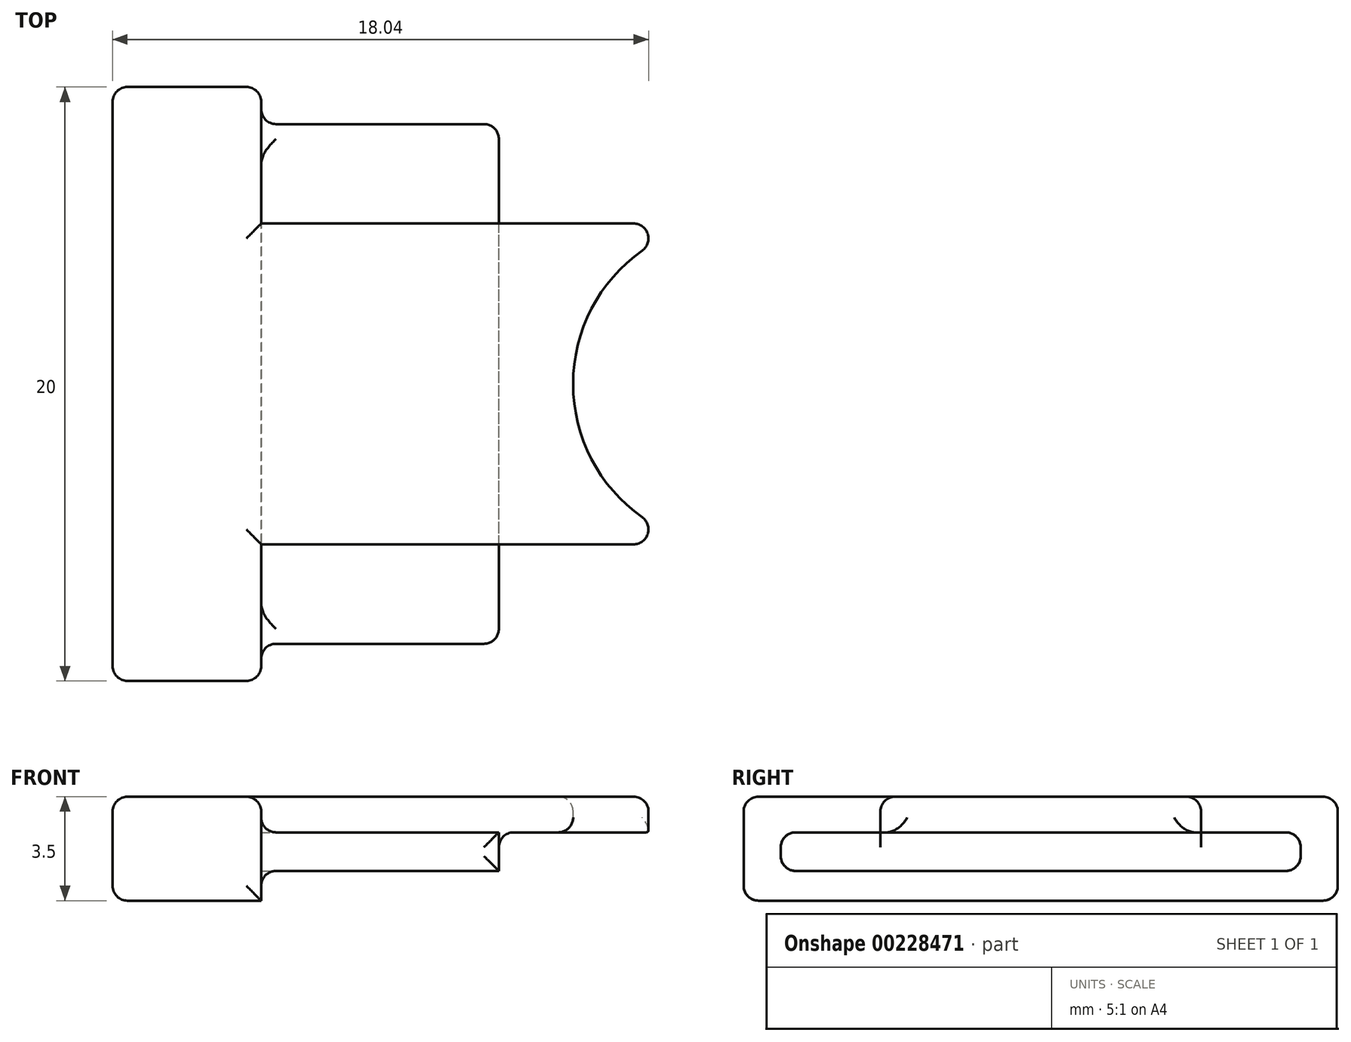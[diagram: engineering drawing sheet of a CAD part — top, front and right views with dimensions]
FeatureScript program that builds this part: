
annotation { "Feature Type Name" : "Feature", "Feature Type Description" : "" }
export const myFeature = defineFeature(function(context is Context, id is Id, definition is map)
    precondition{}
    {
        {
            var Q0;
            Q0=qCreatedBy(makeId("Right.planeOp"),FACE);
            var sketch = newSketch(context, id + "F0", { "sketchPlane" : qUnion([Q0])});
            skLineSegment(sketch, "E0", {"start": v(14.15, 2.5) * mm, "end": v(14.15, 1.3) * mm});
            skLineSegment(sketch, "E1", {"start": v(14.15, 1.3) * mm, "end": v(17.5, 1.3) * mm});
            skLineSegment(sketch, "E2", {"start": v(17.5, 1.3) * mm, "end": v(17.5, 0) * mm});
            skLineSegment(sketch, "E3", {"start": v(17.5, 0) * mm, "end": v(0, 0) * mm});
            skLineSegment(sketch, "E4", {"start": v(0, 0) * mm, "end": v(0, 1.3) * mm});
            skLineSegment(sketch, "E5", {"start": v(0, 1.3) * mm, "end": v(3.35, 1.3) * mm});
            skLineSegment(sketch, "E6", {"start": v(3.35, 1.3) * mm, "end": v(3.35, 2.5) * mm});
            skLineSegment(sketch, "E7", {"start": v(3.35, 2.5) * mm, "end": v(14.15, 2.5) * mm});
            skSolve(sketch);
        }
        {
            var Q0;
            Q0=qSketchRegion(id+"F0",true);
            extrude(context, id + "F1", {"entities" : qUnion([Q0]), "depth" : 16 * mm});
        }
        {
            var Q0;
            Q0=makeQuery(id+"F1.opExtrude","CAP_FACE",FACE,{"disambiguationData":[OSD([sQuery(id+"F0.wireOp",EDGE,"TZ5eURmr-gxjI-tz5t-PajN-iYrOHizqFekN"),sQuery(id+"F0.wireOp",EDGE,"guARKJ44-jrx5-pMLB-4T0B-qmOtUb4eJ82T"),sQuery(id+"F0.wireOp",EDGE,"9YoBGH4t-UvKz-ujqG-odl2-F9yTLTpAYBFK"),sQuery(id+"F0.wireOp",EDGE,"E0"),sQuery(id+"F0.wireOp",EDGE,"E1"),sQuery(id+"F0.wireOp",EDGE,"E2"),sQuery(id+"F0.wireOp",EDGE,"E3"),sQuery(id+"F0.wireOp",EDGE,"E4"),sQuery(id+"F0.wireOp",EDGE,"E5"),sQuery(id+"F0.wireOp",EDGE,"E6"),sQuery(id+"F0.wireOp",EDGE,"JbcaB8nq-M2Nf-0EEa-IcCz-uRVHlxThzm4p"),sQuery(id+"F0.wireOp",EDGE,"coUqNx9z-0dZS-eHZ1-lRqT-18s0Kbs40iIy")])],"isStart":true});
            var sketch = newSketch(context, id + "F2", { "sketchPlane" : qUnion([Q0])});
            skLineSegment(sketch, "E8.bottom", {"start": v(1.25, -1) * mm, "end": v(-18.75, -1) * mm});
            skLineSegment(sketch, "E8.top", {"start": v(1.25, 2.5) * mm, "end": v(-18.75, 2.5) * mm});
            skLineSegment(sketch, "E8.left", {"start": v(1.25, -1) * mm, "end": v(1.25, 2.5) * mm});
            skLineSegment(sketch, "E8.right", {"start": v(-18.75, -1) * mm, "end": v(-18.75, 2.5) * mm});
            skSolve(sketch);
        }
        {
            var Q0;
            Q0=qSketchRegion(id+"F2",true);
            extrude(context, id + "F3", {"entities" : qUnion([Q0]), "operationType" : NewBodyOperationType.ADD, "depth" : 5 * mm});
        }
        {
            var Q0;
            Q0=makeQuery(id+"F3.boolean.opBoolean","MERGE",FACE,{"derivedFrom":[makeQuery(id+"F1.opExtrude","SWEPT_FACE",FACE,{"disambiguationData":[OSD([sQuery(id+"F0.wireOp",EDGE,"9YoBGH4t-UvKz-ujqG-odl2-F9yTLTpAYBFK")])]}),makeQuery(id+"F1.opExtrude","SWEPT_FACE",FACE,{"disambiguationData":[OSD([sQuery(id+"F0.wireOp",EDGE,"coUqNx9z-0dZS-eHZ1-lRqT-18s0Kbs40iIy")])]}),makeQuery(id+"F3.opExtrude","SWEPT_FACE",FACE,{"disambiguationData":[OSD([sQuery(id+"F2.wireOp",EDGE,"E8.top")])]})]});
            var sketch = newSketch(context, id + "F4", { "sketchPlane" : qUnion([Q0])});
            skPoint(sketch, "E9", {"position": v(16, 8.75) * mm});
            skLineSegment(sketch, "E10", {"start": v(16.03, 3.25) * mm, "end": v(16, 14.25) * mm});
            skArc(sketch, "E11", {"start": v(16, 14.25) * mm, "mid": v(10.5, 8.74) * mm, "end": v(16.03, 3.25) * mm});
            skSolve(sketch);
        }
        {
            var Q0;
            Q0=qSketchRegion(id+"F4",true);
            extrude(context, id + "F5", {"entities" : qUnion([Q0]), "operationType" : NewBodyOperationType.REMOVE, "oppositeDirection" : true, "depth" : 5 * mm});
        }
        {
            var Q0;
            {var subQ0=sQuery(id+"F0.wireOp",EDGE,"E3");var subQ1=sQuery(id+"F0.wireOp",EDGE,"E4");var subQ2=sQuery(id+"F0.wireOp",EDGE,"E5");Q0=makeQuery(id+"F5.boolean.opBoolean","SPLIT",FACE,{"disambiguationData":[TD([makeQuery(id+"F1.opExtrude","SWEPT_FACE",FACE,{"disambiguationData":[OSD([subQ1])]})])],"derivedFrom":makeQuery(id+"F1.opExtrude","CAP_FACE",FACE,{"disambiguationData":[OSD([sQuery(id+"F0.wireOp",EDGE,"E0"),sQuery(id+"F0.wireOp",EDGE,"E1"),sQuery(id+"F0.wireOp",EDGE,"E2"),subQ0,subQ1,subQ2,sQuery(id+"F0.wireOp",EDGE,"E6"),sQuery(id+"F0.wireOp",EDGE,"E7")])],"isStart":false})});}
            var sketch = newSketch(context, id + "F6", { "sketchPlane" : qUnion([Q0])});
            skLineSegment(sketch, "E12.bottom", {"start": v(0, 0) * mm, "end": v(17.5, 0) * mm});
            skLineSegment(sketch, "E12.top", {"start": v(0, 1.3) * mm, "end": v(17.5, 1.3) * mm});
            skLineSegment(sketch, "E12.left", {"start": v(0, 0) * mm, "end": v(0, 1.3) * mm});
            skLineSegment(sketch, "E12.right", {"start": v(17.5, 0) * mm, "end": v(17.5, 1.3) * mm});
            skSolve(sketch);
        }
        {
            var Q0;
            Q0 = qSketchRegion(id + "F6", true);
            extrude(context, id + "F7", {"entities" : qUnion([Q0]), "operationType" : NewBodyOperationType.REMOVE, "oppositeDirection" : true, "depth" : 8 * mm});
        }
        {
            var Q0;
            Q0=makeQuery(id+"F1.opExtrude","SWEPT_EDGE",EDGE,{"disambiguationData":[OSD([sQuery(id+"F0.wireOp",EDGE,"E6"),sQuery(id+"F0.wireOp",EDGE,"E7")])]});
            var Q1;
            Q1=makeQuery(id+"F5.boolean.opBoolean","INTERSECT",EDGE,{"derivedFrom":[makeQuery(id+"F1.opExtrude","SWEPT_FACE",FACE,{"disambiguationData":[OSD([sQuery(id+"F0.wireOp",EDGE,"E6")])]}),makeQuery(id+"F5.opExtrude","SWEPT_FACE",FACE,{"disambiguationData":[OSD([sQuery(id+"F4.wireOp",EDGE,"E11")])]})]});
            var Q2;
            Q2=makeQuery(id+"F5.boolean.opBoolean","INTERSECT",EDGE,{"derivedFrom":[makeQuery(id+"F1.opExtrude","SWEPT_FACE",FACE,{"disambiguationData":[OSD([sQuery(id+"F0.wireOp",EDGE,"E0")])]}),makeQuery(id+"F5.opExtrude","SWEPT_FACE",FACE,{"disambiguationData":[OSD([sQuery(id+"F4.wireOp",EDGE,"E11")])]})]});
            var Q3;
            Q3=makeQuery(id+"F5.boolean.opBoolean","INTERSECT",EDGE,{"derivedFrom":[makeQuery(id+"F1.opExtrude","SWEPT_FACE",FACE,{"disambiguationData":[OSD([sQuery(id+"F0.wireOp",EDGE,"E7")])]}),makeQuery(id+"F5.opExtrude","SWEPT_FACE",FACE,{"disambiguationData":[OSD([sQuery(id+"F4.wireOp",EDGE,"E11")])]})]});
            var Q4;
            Q4=makeQuery(id+"F7.boolean.opBoolean","INTERSECT",EDGE,{"derivedFrom":[makeQuery(id+"F5.boolean.opBoolean","COPY",FACE,{"derivedFrom":makeQuery(id+"F5.opExtrude","SWEPT_FACE",FACE,{"disambiguationData":[OSD([sQuery(id+"F4.wireOp",EDGE,"E11")])]})}),makeQuery(id+"F7.opExtrude","SWEPT_FACE",FACE,{"disambiguationData":[OSD([sQuery(id+"F6.wireOp",EDGE,"E12.top")])]})]});
            var Q5;
            Q5=makeQuery(id+"F1.opExtrude","SWEPT_EDGE",EDGE,{"disambiguationData":[OSD([sQuery(id+"F0.wireOp",EDGE,"E0"),sQuery(id+"F0.wireOp",EDGE,"E7")])]});
            var Q6;
            {var subQ0=sQuery(id+"F6.wireOp",EDGE,"E12.top");Q6=makeQuery(id+"F7.boolean.opBoolean","COPY",EDGE,{"disambiguationData":[TD([makeQuery(id+"F1.opExtrude","SWEPT_FACE",FACE,{"disambiguationData":[OSD([sQuery(id+"F0.wireOp",EDGE,"E0")])]}),makeQuery(id+"F1.opExtrude","SWEPT_FACE",FACE,{"disambiguationData":[OSD([sQuery(id+"F0.wireOp",EDGE,"E1")])]}),makeQuery(id+"F1.opExtrude","SWEPT_FACE",FACE,{"disambiguationData":[OSD([sQuery(id+"F0.wireOp",EDGE,"E5")])]}),makeQuery(id+"F1.opExtrude","SWEPT_FACE",FACE,{"disambiguationData":[OSD([sQuery(id+"F0.wireOp",EDGE,"E6")])]}),makeQuery(id+"F7.opExtrude","CAP_FACE",FACE,{"disambiguationData":[OSD([sQuery(id+"F6.wireOp",EDGE,"E12.bottom"),subQ0,sQuery(id+"F6.wireOp",EDGE,"E12.left"),sQuery(id+"F6.wireOp",EDGE,"E12.right")])],"isStart":false}),makeQuery(id+"F7.opExtrude","SWEPT_FACE",FACE,{"disambiguationData":[OSD([subQ0])]})])],"derivedFrom":makeQuery(id+"F7.opExtrude","CAP_EDGE",EDGE,{"disambiguationData":[OSD([subQ0])],"isStart":false})});}
            var Q7;
            Q7=makeQuery(id+"F1.opExtrude","CAP_EDGE",EDGE,{"disambiguationData":[OSD([sQuery(id+"F0.wireOp",EDGE,"E7")])],"isStart":true});
            var Q8;
            Q8=makeQuery(id+"F1.opExtrude","CAP_EDGE",EDGE,{"disambiguationData":[OSD([sQuery(id+"F0.wireOp",EDGE,"E5")])],"isStart":true});
            var Q9;
            Q9=makeQuery(id+"F1.opExtrude","CAP_EDGE",EDGE,{"disambiguationData":[OSD([sQuery(id+"F0.wireOp",EDGE,"E4")])],"isStart":true});
            var Q10;
            Q10=makeQuery(id+"F1.opExtrude","CAP_EDGE",EDGE,{"disambiguationData":[OSD([sQuery(id+"F0.wireOp",EDGE,"E3")])],"isStart":true});
            var Q11;
            Q11=makeQuery(id+"F1.opExtrude","CAP_EDGE",EDGE,{"disambiguationData":[OSD([sQuery(id+"F0.wireOp",EDGE,"E2")])],"isStart":true});
            var Q12;
            Q12=makeQuery(id+"F1.opExtrude","CAP_EDGE",EDGE,{"disambiguationData":[OSD([sQuery(id+"F0.wireOp",EDGE,"E1")])],"isStart":true});
            var Q13;
            Q13=makeQuery(id+"F3.opExtrude","CAP_FACE",FACE,{"disambiguationData":[OSD([sQuery(id+"F2.wireOp",EDGE,"E8.bottom"),sQuery(id+"F2.wireOp",EDGE,"E8.top"),sQuery(id+"F2.wireOp",EDGE,"E8.left"),sQuery(id+"F2.wireOp",EDGE,"E8.right")])],"isStart":false});
            var Q14;
            Q14=makeQuery(id+"F3.opExtrude","SWEPT_FACE",FACE,{"disambiguationData":[OSD([sQuery(id+"F2.wireOp",EDGE,"E8.left")])]});
            var Q15;
            Q15=makeQuery(id+"F3.opExtrude","SWEPT_FACE",FACE,{"disambiguationData":[OSD([sQuery(id+"F2.wireOp",EDGE,"E8.right")])]});
            var Q16;
            Q16=makeQuery(id+"F1.opExtrude","SWEPT_FACE",FACE,{"disambiguationData":[OSD([sQuery(id+"F0.wireOp",EDGE,"E2")])]});
            var Q17;
            Q17=makeQuery(id+"F1.opExtrude","SWEPT_FACE",FACE,{"disambiguationData":[OSD([sQuery(id+"F0.wireOp",EDGE,"E4")])]});
            var Q18;
            Q18=makeQuery(id+"F7.boolean.opBoolean","COPY",EDGE,{"derivedFrom":makeQuery(id+"F7.opExtrude","CAP_EDGE",EDGE,{"disambiguationData":[OSD([sQuery(id+"F6.wireOp",EDGE,"E12.bottom")])],"isStart":false})});
            var Q19;
            {var subQ0=sQuery(id+"F2.wireOp",EDGE,"E8.top");Q19=makeQuery(id+"F3.boolean.opBoolean","SPLIT",EDGE,{"disambiguationData":[TD([makeQuery(id+"F1.opExtrude","SWEPT_FACE",FACE,{"disambiguationData":[OSD([sQuery(id+"F0.wireOp",EDGE,"E6")])]})])],"derivedFrom":makeQuery(id+"F3.opExtrude","CAP_EDGE",EDGE,{"disambiguationData":[OSD([subQ0])],"isStart":true})});}
            var Q20;
            {var subQ0=sQuery(id+"F2.wireOp",EDGE,"E8.top");Q20=makeQuery(id+"F3.boolean.opBoolean","SPLIT",EDGE,{"disambiguationData":[TD([makeQuery(id+"F1.opExtrude","SWEPT_FACE",FACE,{"disambiguationData":[OSD([sQuery(id+"F0.wireOp",EDGE,"E0")])]})])],"derivedFrom":makeQuery(id+"F3.opExtrude","CAP_EDGE",EDGE,{"disambiguationData":[OSD([subQ0])],"isStart":true})});}
            var Q21;
            Q21=makeQuery(id+"F1.opExtrude","CAP_EDGE",EDGE,{"disambiguationData":[OSD([sQuery(id+"F0.wireOp",EDGE,"E6")])],"isStart":true});
            var Q22;
            Q22=makeQuery(id+"F1.opExtrude","CAP_EDGE",EDGE,{"disambiguationData":[OSD([sQuery(id+"F0.wireOp",EDGE,"E0")])],"isStart":true});
            var Q23;
            Q23=makeQuery(id+"F5.boolean.opBoolean","COPY",EDGE,{"derivedFrom":makeQuery(id+"F5.opExtrude","CAP_EDGE",EDGE,{"disambiguationData":[OSD([sQuery(id+"F4.wireOp",EDGE,"E11")])],"isStart":true})});
            fillet(context, id + "F8", {"entities" : qUnion([Q0, Q1, Q2, Q3, Q4, Q5, Q6, Q7, Q8, Q9, Q10, Q11, Q12, Q13, Q14, Q15, Q16, Q17, Q18, Q19, Q20, Q21, Q22, Q23]), "radius" : 0.5 * mm, "tangentPropagation" : true, "allowEdgeOverflow" : false});
        }
    });
